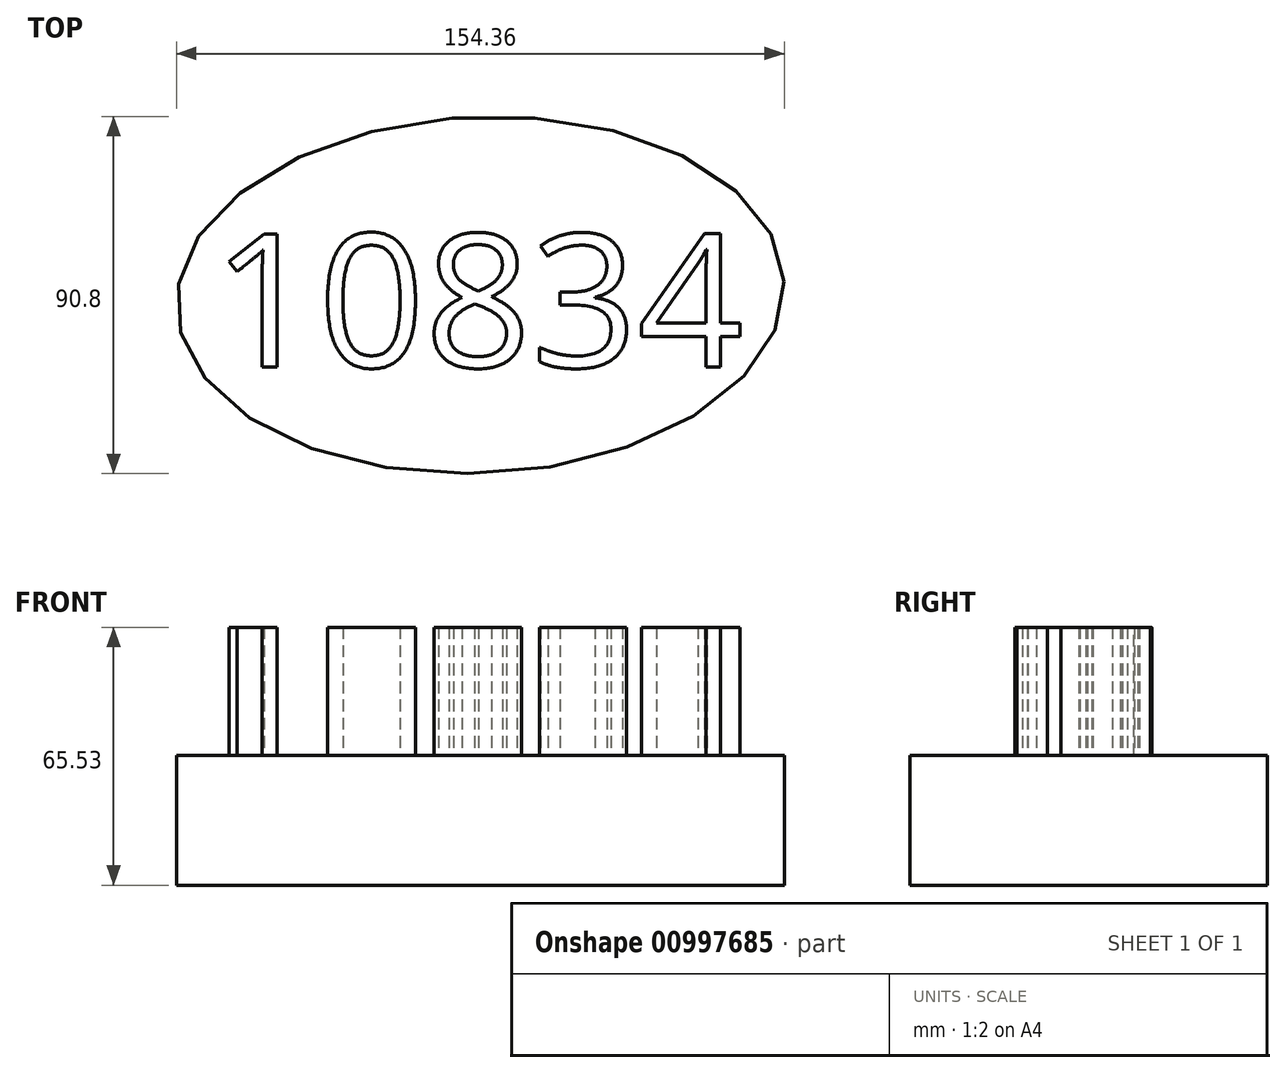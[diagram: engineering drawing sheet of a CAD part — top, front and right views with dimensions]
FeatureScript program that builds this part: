
annotation { "Feature Type Name" : "Feature", "Feature Type Description" : "" }
export const myFeature = defineFeature(function(context is Context, id is Id, definition is map)
    precondition{}
    {
        {
            var Q0;
            Q0=qCreatedBy(makeId("Top.planeOp"),FACE);
            var sketch = newSketch(context, id + "F0", { "sketchPlane" : qUnion([Q0])});
            skEllipse(sketch, "E0", {"center": v(0, 0) * mm, "majorRadius": 77.23 * mm, "minorRadius": 45.32 * mm, "majorAxis": v(1, 0.04)});
            skSolve(sketch);
        }
        {
            var Q0;
            Q0=makeQuery(id+"F0.imprint","IMPRINT",FACE,{"disambiguationData":[TD([[makeQuery(id+"F0.imprint","IMPRINT",EDGE,{"derivedFrom":sQuery(id+"F0.wireOp",EDGE,"E0")}),1.0]])]});
            extrude(context, id + "F1", {"entities" : qUnion([Q0]), "oppositeDirection" : true, "depth" : 33.02 * mm, "offsetDistance" : 25.4 * mm});
        }
        {
            var Q0;
            Q0=makeQuery(id+"F1.opExtrude","CAP_FACE",FACE,{"disambiguationData":[OSD([sQuery(id+"F0.wireOp",EDGE,"E0")])],"isStart":true});
            var sketch = newSketch(context, id + "F2", { "sketchPlane" : qUnion([Q0])});
            skText(sketch, "E1", { "text": "10834", "fontName": "OpenSans-Regular.ttf"});
            const initialGuessF2  = {"E1": [-0.06819, -0.01829, 1, 0, 0.03403]};
            skSetInitialGuess(sketch, initialGuessF2);
            skSolve(sketch);
        }
        {
            var Q0;
            Q0 = qSketchRegion(id + "F2", true);
            extrude(context, id + "F3", {"entities" : qUnion([Q0]), "operationType" : NewBodyOperationType.ADD, "depth" : 32.5 * mm, "offsetDistance" : 25.4 * mm});
        }
    });
